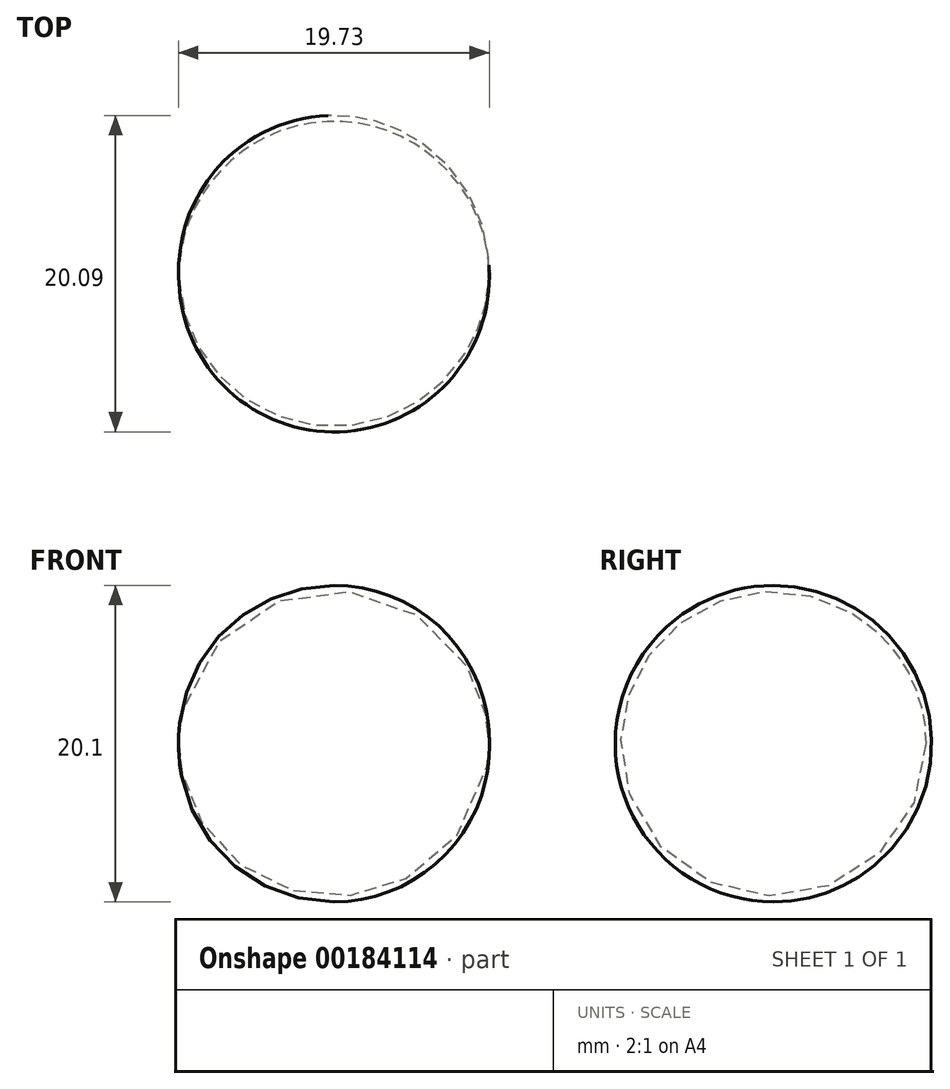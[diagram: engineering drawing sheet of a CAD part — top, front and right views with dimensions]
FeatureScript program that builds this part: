
annotation { "Feature Type Name" : "Feature", "Feature Type Description" : "" }
export const myFeature = defineFeature(function(context is Context, id is Id, definition is map)
    precondition{}
    {
        {
            var Q0;
            Q0=qCreatedBy(makeId("Top.planeOp"),FACE);
            var sketch = newSketch(context, id + "F0", { "sketchPlane" : qUnion([Q0])});
            skArc(sketch, "E0", {"start": v(-26.37, 24.09) * mm, "mid": v(-36.58, 33.4) * mm, "end": v(-46.08, 23.36) * mm});
            skLineSegment(sketch, "E1", {"start": v(-46.08, 23.36) * mm, "end": v(-26.37, 24.09) * mm});
            skSolve(sketch);
        }
        {
            var Q0;
            Q0=makeQuery(id+"F0.imprint","IMPRINT",FACE,{"disambiguationData":[TD([[makeQuery(id+"F0.imprint","IMPRINT",EDGE,{"derivedFrom":sQuery(id+"F0.wireOp",EDGE,"E0")}),1.0]])]});
            var Q1;
            Q1=sQuery(id+"F0.wireOp",EDGE,"E1");
            revolve(context, id + "F1", {"entities" : qUnion([Q0]), "axis" : qUnion([Q1]), "revolveType" : RevolveType.FULL});
        }
    });
